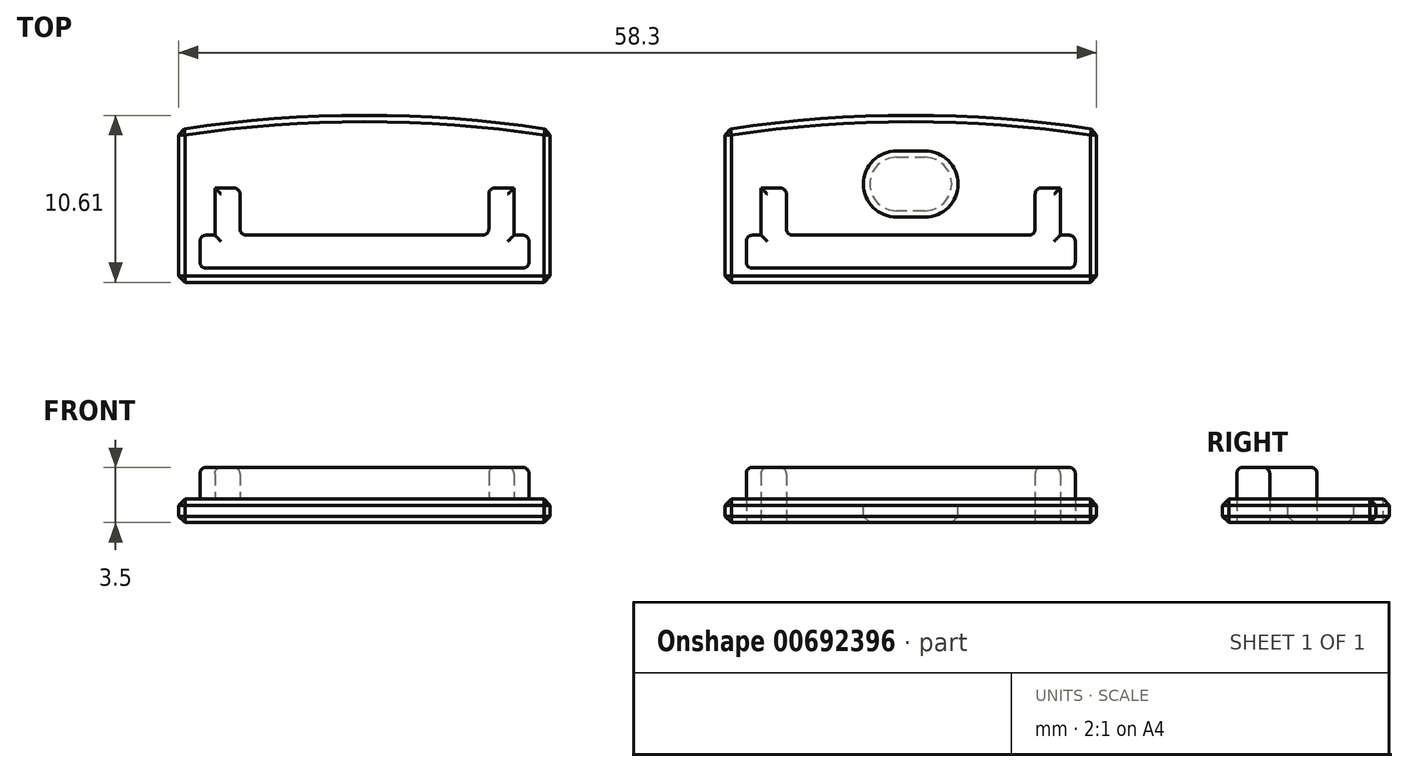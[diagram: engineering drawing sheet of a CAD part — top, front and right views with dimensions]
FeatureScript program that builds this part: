
annotation { "Feature Type Name" : "Feature", "Feature Type Description" : "" }
export const myFeature = defineFeature(function(context is Context, id is Id, definition is map)
    precondition{}
    {
        {
            var Q0;
            Q0=qCreatedBy(makeId("Top.planeOp"),FACE);
            var sketch = newSketch(context, id + "F0", { "sketchPlane" : qUnion([Q0])});
            skLineSegment(sketch, "E0.bottom", {"start": v(11.8, -4.85) * mm, "end": v(-11.8, -4.85) * mm});
            skLineSegment(sketch, "E0.top", {"start": v(11.8, 4.85) * mm, "end": v(-11.8, 4.85) * mm, "construction": true});
            skLineSegment(sketch, "E0.left", {"start": v(11.8, -4.85) * mm, "end": v(11.8, 4.85) * mm});
            skLineSegment(sketch, "E0.right", {"start": v(-11.8, -4.85) * mm, "end": v(-11.8, 4.85) * mm});
            skPoint(sketch, "E0.middle", {"position": v(0, 0) * mm});
            skLineSegment(sketch, "E1", {"start": v(-11.8, 5.76) * mm, "end": v(11.8, 5.76) * mm, "construction": true});
            skArc(sketch, "E2", {"start": v(-11.8, 4.85) * mm, "mid": v(0, -148.16) * mm, "end": v(11.8, 4.85) * mm, "construction": true});
            skArc(sketch, "E3", {"start": v(11.8, 4.85) * mm, "mid": v(0, 5.76) * mm, "end": v(-11.8, 4.85) * mm});
            skSolve(sketch);
        }
        {
            var Q0;
            Q0=makeQuery(id+"F0.imprint","IMPRINT",FACE,{"disambiguationData":[TD([[makeQuery(id+"F0.imprint","IMPRINT",EDGE,{"derivedFrom":sQuery(id+"F0.wireOp",EDGE,"E0.bottom")}),-1.0]])]});
            extrude(context, id + "F1", {"entities" : qUnion([Q0]), "depth" : 1.5 * mm, "offsetDistance" : 25 * mm});
        }
        {
            var Q0;
            Q0=makeQuery(id+"F1.opExtrude","CAP_FACE",FACE,{"disambiguationData":[OSD([sQuery(id+"F0.wireOp",EDGE,"E0.bottom"),sQuery(id+"F0.wireOp",EDGE,"E0.left"),sQuery(id+"F0.wireOp",EDGE,"E0.right"),sQuery(id+"F0.wireOp",EDGE,"E3")])],"isStart":false});
            var sketch = newSketch(context, id + "F2", { "sketchPlane" : qUnion([Q0])});
            skPoint(sketch, "E4.0", {"position": v(-11.8, -4.85) * mm});
            skLineSegment(sketch, "E5.bottom", {"start": v(-10.45, -3.95) * mm, "end": v(10.45, -3.95) * mm});
            skLineSegment(sketch, "E5.top", {"start": v(-10.45, -1.85) * mm, "end": v(-9.5, -1.85) * mm});
            skLineSegment(sketch, "E5.left", {"start": v(-10.45, -3.95) * mm, "end": v(-10.45, -1.85) * mm});
            skLineSegment(sketch, "E5.right", {"start": v(10.45, -3.95) * mm, "end": v(10.45, -1.85) * mm});
            skPoint(sketch, "E5.middle", {"position": v(0, -2.9) * mm});
            skLineSegment(sketch, "E6", {"start": v(0, 0) * mm, "end": v(0, 1.6) * mm, "construction": true});
            skLineSegment(sketch, "E7.bottom", {"start": v(-9.5, -1.85) * mm, "end": v(-7.9, -1.85) * mm, "construction": true});
            skLineSegment(sketch, "E7.top", {"start": v(-9.5, 1.15) * mm, "end": v(-7.9, 1.15) * mm});
            skLineSegment(sketch, "E7.left", {"start": v(-9.5, -1.85) * mm, "end": v(-9.5, 1.15) * mm});
            skLineSegment(sketch, "E7.right", {"start": v(-7.9, -1.85) * mm, "end": v(-7.9, 1.15) * mm});
            skPoint(sketch, "E7.middle", {"position": v(-8.7, -0.35) * mm});
            skLineSegment(sketch, "E8.MirrorCS", {"start": v(7.9, -1.85) * mm, "end": v(7.9, 1.15) * mm});
            skLineSegment(sketch, "E9.MirrorCS", {"start": v(9.5, 1.15) * mm, "end": v(7.9, 1.15) * mm});
            skLineSegment(sketch, "E10.MirrorCS", {"start": v(9.5, -1.85) * mm, "end": v(9.5, 1.15) * mm});
            skLineSegment(sketch, "E11.MirrorCS", {"start": v(9.5, -1.85) * mm, "end": v(7.9, -1.85) * mm, "construction": true});
            skLineSegment(sketch, "E12", {"start": v(-7.9, -1.85) * mm, "end": v(7.9, -1.85) * mm});
            skLineSegment(sketch, "E13", {"start": v(7.9, -1.85) * mm, "end": v(9.5, -1.85) * mm, "construction": true});
            skLineSegment(sketch, "E14", {"start": v(9.5, -1.85) * mm, "end": v(10.45, -1.85) * mm});
            skSolve(sketch);
        }
        {
            var Q0;
            Q0=makeQuery(id+"F2.imprint","IMPRINT",FACE,{"disambiguationData":[TD([[makeQuery(id+"F2.imprint","IMPRINT",EDGE,{"derivedFrom":sQuery(id+"F2.wireOp",EDGE,"E5.bottom")}),1.0]])]});
            extrude(context, id + "F3", {"entities" : qUnion([Q0]), "operationType" : NewBodyOperationType.ADD, "depth" : 2 * mm, "offsetDistance" : 25 * mm});
        }
        {
            var Q0;
            Q0=makeQuery(id+"F3.opExtrude","SWEPT_EDGE",EDGE,{"disambiguationData":[OSD([sQuery(id+"F2.wireOp",EDGE,"E7.top"),sQuery(id+"F2.wireOp",EDGE,"E7.right")])]});
            var Q1;
            Q1=makeQuery(id+"F3.opExtrude","SWEPT_EDGE",EDGE,{"disambiguationData":[OSD([sQuery(id+"F2.wireOp",EDGE,"E7.right"),sQuery(id+"F2.wireOp",EDGE,"E12")])]});
            var Q2;
            Q2=makeQuery(id+"F3.opExtrude","CAP_EDGE",EDGE,{"disambiguationData":[OSD([sQuery(id+"F2.wireOp",EDGE,"E12")])],"isStart":true});
            var Q3;
            Q3=makeQuery(id+"F3.opExtrude","CAP_EDGE",EDGE,{"disambiguationData":[OSD([sQuery(id+"F2.wireOp",EDGE,"E7.right")])],"isStart":true});
            var Q4;
            Q4=makeQuery(id+"F3.opExtrude","SWEPT_EDGE",EDGE,{"disambiguationData":[OSD([sQuery(id+"F2.wireOp",EDGE,"E8.MirrorCS"),sQuery(id+"F2.wireOp",EDGE,"E12")])]});
            var Q5;
            Q5=makeQuery(id+"F3.opExtrude","CAP_EDGE",EDGE,{"disambiguationData":[OSD([sQuery(id+"F2.wireOp",EDGE,"E8.MirrorCS")])],"isStart":true});
            var Q6;
            Q6=makeQuery(id+"F3.opExtrude","SWEPT_EDGE",EDGE,{"disambiguationData":[OSD([sQuery(id+"F2.wireOp",EDGE,"E8.MirrorCS"),sQuery(id+"F2.wireOp",EDGE,"E9.MirrorCS")])]});
            var Q7;
            Q7=makeQuery(id+"F3.opExtrude","SWEPT_EDGE",EDGE,{"disambiguationData":[OSD([sQuery(id+"F2.wireOp",EDGE,"E5.top"),sQuery(id+"F2.wireOp",EDGE,"E5.left")])]});
            var Q8;
            Q8=makeQuery(id+"F3.opExtrude","SWEPT_EDGE",EDGE,{"disambiguationData":[OSD([sQuery(id+"F2.wireOp",EDGE,"E5.bottom"),sQuery(id+"F2.wireOp",EDGE,"E5.left")])]});
            var Q9;
            Q9=makeQuery(id+"F3.opExtrude","SWEPT_EDGE",EDGE,{"disambiguationData":[OSD([sQuery(id+"F2.wireOp",EDGE,"E5.bottom"),sQuery(id+"F2.wireOp",EDGE,"E5.right")])]});
            var Q10;
            Q10=makeQuery(id+"F3.opExtrude","SWEPT_EDGE",EDGE,{"disambiguationData":[OSD([sQuery(id+"F2.wireOp",EDGE,"E5.right"),sQuery(id+"F2.wireOp",EDGE,"E14")])]});
            var Q11;
            Q11=makeQuery(id+"F3.opExtrude","CAP_FACE",FACE,{"disambiguationData":[OSD([sQuery(id+"F2.wireOp",EDGE,"E5.bottom"),sQuery(id+"F2.wireOp",EDGE,"E5.top"),sQuery(id+"F2.wireOp",EDGE,"E5.left"),sQuery(id+"F2.wireOp",EDGE,"E5.right"),sQuery(id+"F2.wireOp",EDGE,"E7.top"),sQuery(id+"F2.wireOp",EDGE,"E7.left"),sQuery(id+"F2.wireOp",EDGE,"E7.right"),sQuery(id+"F2.wireOp",EDGE,"E8.MirrorCS"),sQuery(id+"F2.wireOp",EDGE,"E9.MirrorCS"),sQuery(id+"F2.wireOp",EDGE,"E10.MirrorCS"),sQuery(id+"F2.wireOp",EDGE,"E12"),sQuery(id+"F2.wireOp",EDGE,"E14")])],"isStart":false});
            fillet(context, id + "F4", {"entities" : qUnion([Q0, Q1, Q2, Q3, Q4, Q5, Q6, Q7, Q8, Q9, Q10, Q11]), "radius" : 0.4 * mm, "tangentPropagation" : true, "allowEdgeOverflow" : false});
        }
        {
            var Q0;
            Q0=makeQuery(id+"F1.opExtrude","CAP_FACE",FACE,{"disambiguationData":[OSD([sQuery(id+"F0.wireOp",EDGE,"E0.bottom"),sQuery(id+"F0.wireOp",EDGE,"E0.left"),sQuery(id+"F0.wireOp",EDGE,"E0.right"),sQuery(id+"F0.wireOp",EDGE,"E3")])],"isStart":true});
            var Q1;
            Q1=makeQuery(id+"F1.opExtrude","SWEPT_EDGE",EDGE,{"disambiguationData":[OSD([sQuery(id+"F0.wireOp",EDGE,"E0.bottom"),sQuery(id+"F0.wireOp",EDGE,"E0.right")])]});
            var Q2;
            Q2=makeQuery(id+"F1.opExtrude","SWEPT_EDGE",EDGE,{"disambiguationData":[OSD([sQuery(id+"F0.wireOp",EDGE,"E0.bottom"),sQuery(id+"F0.wireOp",EDGE,"E0.left")])]});
            var Q3;
            Q3=makeQuery(id+"F1.opExtrude","SWEPT_EDGE",EDGE,{"disambiguationData":[OSD([sQuery(id+"F0.wireOp",EDGE,"E0.left"),sQuery(id+"F0.wireOp",EDGE,"E3")])]});
            var Q4;
            Q4=makeQuery(id+"F1.opExtrude","SWEPT_EDGE",EDGE,{"disambiguationData":[OSD([sQuery(id+"F0.wireOp",EDGE,"E0.right"),sQuery(id+"F0.wireOp",EDGE,"E3")])]});
            var Q5;
            Q5=makeQuery(id+"F1.opExtrude","CAP_EDGE",EDGE,{"disambiguationData":[OSD([sQuery(id+"F0.wireOp",EDGE,"E3")])],"isStart":false});
            var Q6;
            Q6=makeQuery(id+"F1.opExtrude","CAP_EDGE",EDGE,{"disambiguationData":[OSD([sQuery(id+"F0.wireOp",EDGE,"E0.right")])],"isStart":false});
            var Q7;
            Q7=makeQuery(id+"F1.opExtrude","CAP_EDGE",EDGE,{"disambiguationData":[OSD([sQuery(id+"F0.wireOp",EDGE,"E0.bottom")])],"isStart":false});
            var Q8;
            Q8=makeQuery(id+"F1.opExtrude","CAP_EDGE",EDGE,{"disambiguationData":[OSD([sQuery(id+"F0.wireOp",EDGE,"E0.left")])],"isStart":false});
            chamfer(context, id + "F5", {"entities" : qUnion([Q0, Q1, Q2, Q3, Q4, Q5, Q6, Q7, Q8]), "width" : 0.4 * mm, "tangentPropagation" : true});
        }
        {
            var Q0;
            Q0=makeQuery(id+"F1.opExtrude","SWEPT_BODY",BODY,{"disambiguationData":[OSD([sQuery(id+"F0.wireOp",EDGE,"E0.bottom"),sQuery(id+"F0.wireOp",EDGE,"E0.left"),sQuery(id+"F0.wireOp",EDGE,"E0.right"),sQuery(id+"F0.wireOp",EDGE,"E3")])]});
            transform(context, id + "F6", {"entities" : qUnion([Q0]), "transformType" : TransformType.TRANSLATION_3D, "dx" : 34.7 * mm, "dy" : 0 * mm, "dz" : 0 * mm, "makeCopy" : true});
        }
        {
            var Q0;
            Q0=makeQuery(id+"F6.opPattern","COPY",FACE,{"derivedFrom":makeQuery(id+"F1.opExtrude","CAP_FACE",FACE,{"disambiguationData":[OSD([sQuery(id+"F0.wireOp",EDGE,"E0.bottom"),sQuery(id+"F0.wireOp",EDGE,"E0.left"),sQuery(id+"F0.wireOp",EDGE,"E0.right"),sQuery(id+"F0.wireOp",EDGE,"E3")])],"isStart":false}),"instanceName":"1"});
            var sketch = newSketch(context, id + "F7", { "sketchPlane" : qUnion([Q0])});
            skPoint(sketch, "E15", {"position": v(34.7, 1.4) * mm});
            skPoint(sketch, "E15.positionSnap0", {"position": v(34.7, -4.45) * mm});
            skPoint(sketch, "E15.positionSnap1", {"position": v(23.3, 0.03) * mm});
            skLineSegment(sketch, "E16", {"start": v(33.8, 1.4) * mm, "end": v(35.6, 1.4) * mm, "construction": true});
            skArc(sketch, "E17.0.startCap", {"start": v(33.8, -0.7) * mm, "mid": v(31.7, 1.4) * mm, "end": v(33.8, 3.5) * mm});
            skArc(sketch, "E17.0.endCap", {"start": v(35.6, 3.5) * mm, "mid": v(37.7, 1.4) * mm, "end": v(35.6, -0.7) * mm});
            skLineSegment(sketch, "E17.0.left", {"start": v(33.8, 3.5) * mm, "end": v(35.6, 3.5) * mm});
            skLineSegment(sketch, "E17.0.right", {"start": v(33.8, -0.7) * mm, "end": v(35.6, -0.7) * mm});
            skSolve(sketch);
        }
        {
            var Q0;
            Q0=makeQuery(id+"F7.imprint","IMPRINT",FACE,{"disambiguationData":[TD([[makeQuery(id+"F7.imprint","IMPRINT",EDGE,{"derivedFrom":sQuery(id+"F7.wireOp",EDGE,"E17.0.startCap")}),-1.0]])]});
            extrude(context, id + "F8", {"entities" : qUnion([Q0]), "operationType" : NewBodyOperationType.REMOVE, "endBound" : BoundingType.THROUGH_ALL, "oppositeDirection" : true, "depth" : 25 * mm, "offsetDistance" : 25 * mm});
        }
        {
            var Q0;
            Q0=makeQuery(id+"F8.boolean.opBoolean","COPY",EDGE,{"derivedFrom":makeQuery(id+"F8.opExtrude","CAP_EDGE",EDGE,{"disambiguationData":[OSD([sQuery(id+"F7.wireOp",EDGE,"E17.0.startCap")])],"isStart":true})});
            var Q1;
            Q1=makeQuery(id+"F8.boolean.opBoolean","INTERSECT",EDGE,{"derivedFrom":[makeQuery(id+"F6.opPattern","COPY",FACE,{"derivedFrom":makeQuery(id+"F1.opExtrude","CAP_FACE",FACE,{"disambiguationData":[OSD([sQuery(id+"F0.wireOp",EDGE,"E0.bottom"),sQuery(id+"F0.wireOp",EDGE,"E0.left"),sQuery(id+"F0.wireOp",EDGE,"E0.right"),sQuery(id+"F0.wireOp",EDGE,"E3")])],"isStart":true}),"instanceName":"1"}),makeQuery(id+"F8.opExtrude","SWEPT_FACE",FACE,{"disambiguationData":[OSD([sQuery(id+"F7.wireOp",EDGE,"E17.0.endCap")])]})]});
            chamfer(context, id + "F9", {"entities" : qUnion([Q0, Q1]), "width" : 0.4 * mm, "tangentPropagation" : true});
        }
    });
